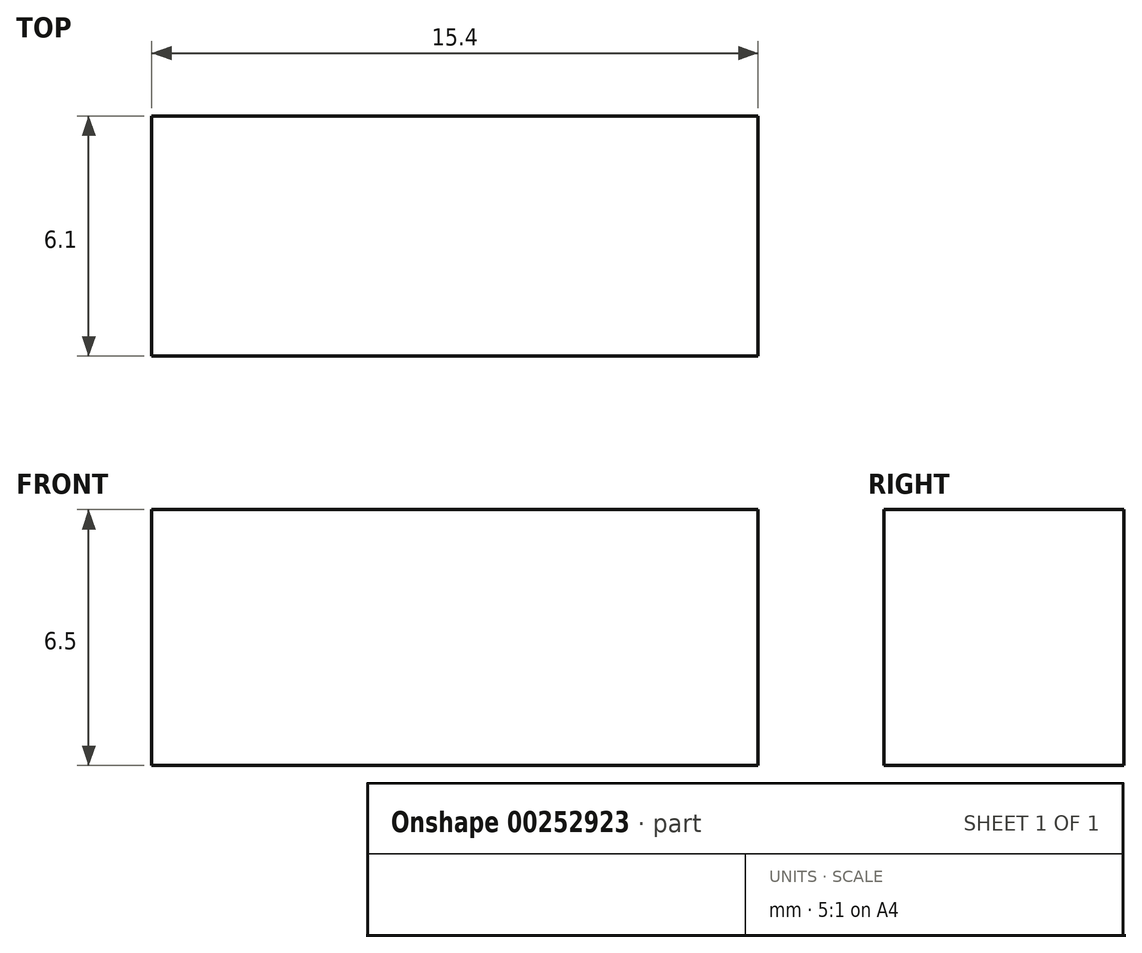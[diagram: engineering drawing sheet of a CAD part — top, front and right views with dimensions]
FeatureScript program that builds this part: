
annotation { "Feature Type Name" : "Feature", "Feature Type Description" : "" }
export const myFeature = defineFeature(function(context is Context, id is Id, definition is map)
    precondition{}
    {
        {
            var Q0;
            Q0=qCreatedBy(makeId("Top.planeOp"),FACE);
            var sketch = newSketch(context, id + "F6", { "sketchPlane" : qUnion([Q0])});
            skLineSegment(sketch, "E0.bottom", {"start": v(-8.2, 4.57) * mm, "end": v(5.2, 4.57) * mm});
            skLineSegment(sketch, "E0.top", {"start": v(-8.2, 0.47) * mm, "end": v(5.2, 0.47) * mm});
            skLineSegment(sketch, "E0.left", {"start": v(-8.2, 4.57) * mm, "end": v(-8.2, 0.47) * mm});
            skLineSegment(sketch, "E0.right", {"start": v(5.2, 4.57) * mm, "end": v(5.2, 0.47) * mm});
            skSolve(sketch);
        }
        {
            var Q0;
            Q0=makeQuery(id+"F6.imprint","IMPRINT",FACE,{"disambiguationData":[TD([[makeQuery(id+"F6.imprint","IMPRINT",EDGE,{"derivedFrom":sQuery(id+"F6.wireOp",EDGE,"E0.bottom")}),-1.0]])]});
            extrude(context, id + "F0", {"entities" : qUnion([Q0]), "depth" : 6.5 * mm});
        }
        {
            var Q0;
            Q0=makeQuery(id+"F0.opExtrude","SWEPT_FACE",FACE,{"disambiguationData":[OSD([sQuery(id+"F6.wireOp",EDGE,"E0.bottom")])]});
            extrude(context, id + "F1", {"entities" : qUnion([Q0]), "operationType" : NewBodyOperationType.ADD, "depth" : 1 * mm});
        }
        {
            var Q0;
            {var subQ0=sQuery(id+"F6.wireOp",EDGE,"E0.right");Q0=makeQuery(id+"F1.boolean.opBoolean","MERGE",FACE,{"derivedFrom":[makeQuery(id+"F0.opExtrude","SWEPT_FACE",FACE,{"disambiguationData":[OSD([subQ0])]}),makeQuery(id+"F1.opExtrude","SWEPT_FACE",FACE,{"disambiguationData":[OSD([sQuery(id+"F6.wireOp",EDGE,"E0.bottom"),subQ0])]})]});}
            extrude(context, id + "F2", {"entities" : qUnion([Q0]), "operationType" : NewBodyOperationType.ADD, "depth" : 1 * mm});
        }
        {
            var Q0;
            {var subQ0=sQuery(id+"F6.wireOp",EDGE,"E0.left");Q0=makeQuery(id+"F1.boolean.opBoolean","MERGE",FACE,{"derivedFrom":[makeQuery(id+"F0.opExtrude","SWEPT_FACE",FACE,{"disambiguationData":[OSD([subQ0])]}),makeQuery(id+"F1.opExtrude","SWEPT_FACE",FACE,{"disambiguationData":[OSD([sQuery(id+"F6.wireOp",EDGE,"E0.bottom"),subQ0])]})]});}
            var sketch = newSketch(context, id + "F3", { "sketchPlane" : qUnion([Q0])});
            skSolve(sketch);
        }
        {
            var Q0;
            Q0 = qSketchRegion(id + "F3", true);
            var Q1;
            {var subQ0=sQuery(id+"F6.wireOp",EDGE,"E0.top");Q1=makeQuery(id+"F2.boolean.opBoolean","MERGE",FACE,{"derivedFrom":[makeQuery(id+"F0.opExtrude","SWEPT_FACE",FACE,{"disambiguationData":[OSD([subQ0])]}),makeQuery(id+"F2.opExtrude","SWEPT_FACE",FACE,{"disambiguationData":[OSD([subQ0,sQuery(id+"F6.wireOp",EDGE,"E0.right")])]})]});}
            extrude(context, id + "F4", {"entities" : qUnion([Q0, Q1]), "operationType" : NewBodyOperationType.ADD, "depth" : 1 * mm});
        }
        {
            var Q0;
            {var subQ0=sQuery(id+"F6.wireOp",EDGE,"E0.left");Q0=makeQuery(id+"F3.imprint","IMPRINT",FACE,{"disambiguationData":[TD([[makeQuery(id+"F3.imprint","IMPRINT",EDGE,{"derivedFrom":makeQuery(id+"F0.opExtrude","SWEPT_EDGE",EDGE,{"disambiguationData":[OSD([sQuery(id+"F6.wireOp",EDGE,"E0.top"),subQ0])]})}),-1.0]])]});}
            var Q1;
            {var subQ0=sQuery(id+"F6.wireOp",EDGE,"E0.left");Q1=makeQuery(id+"F4.boolean.opBoolean","MERGE",FACE,{"derivedFrom":[makeQuery(id+"F1.boolean.opBoolean","MERGE",FACE,{"derivedFrom":[makeQuery(id+"F0.opExtrude","SWEPT_FACE",FACE,{"disambiguationData":[OSD([subQ0])]}),makeQuery(id+"F1.opExtrude","SWEPT_FACE",FACE,{"disambiguationData":[OSD([sQuery(id+"F6.wireOp",EDGE,"E0.bottom"),subQ0])]})]}),makeQuery(id+"F4.opExtrude","SWEPT_FACE",FACE,{"disambiguationData":[OSD([sQuery(id+"F6.wireOp",EDGE,"E0.top"),subQ0])]})]});}
            extrude(context, id + "F7", {"entities" : qUnion([Q0, Q1]), "operationType" : NewBodyOperationType.ADD, "depth" : 1 * mm});
        }
    });
